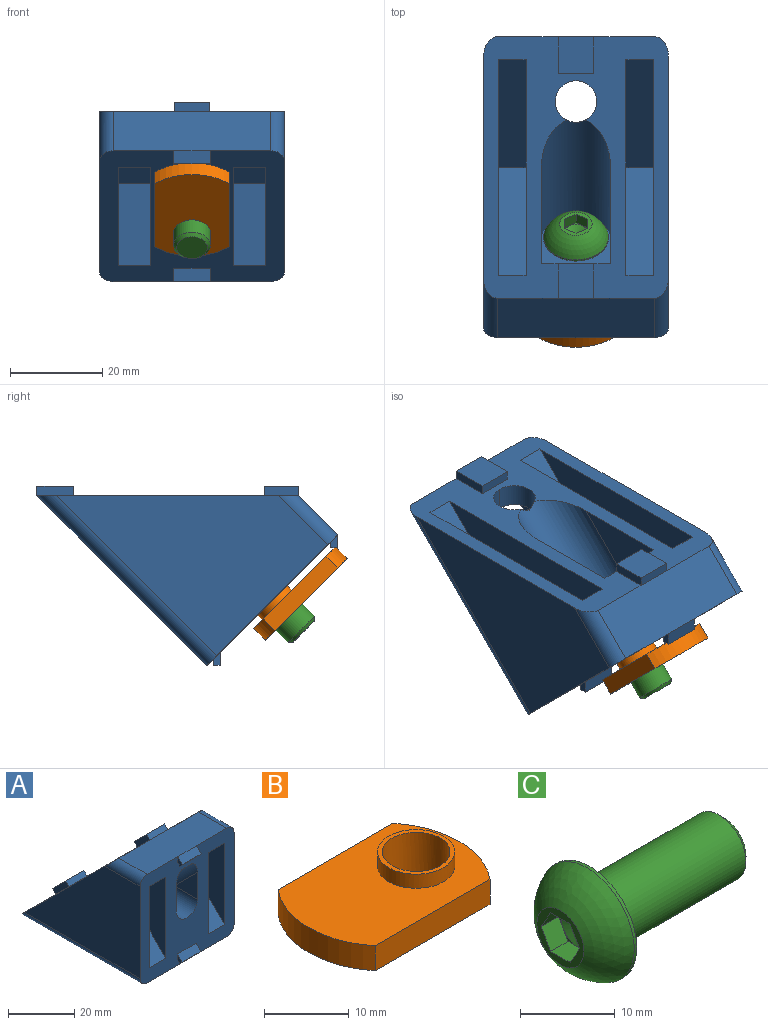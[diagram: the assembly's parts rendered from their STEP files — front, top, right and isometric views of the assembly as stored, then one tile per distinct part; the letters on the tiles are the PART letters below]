
ASSEMBLY  parts=3 mates=2
PART A: 65 faces, bbox 40x55.6x46.7 mm
  f0: plane 7.7x5.25mm, normal (0,0.71,0.71), area 57.2mm2, adj f2,f14,f18,f19
  f1: plane 8x1.06mm, normal (0,-0.71,-0.71), area 12mm2, adj f29,f30,f31,f32
  f2: plane 7.7x1.41mm, normal (0,-0.71,0.71), area 15.4mm2, adj f0,f14,f18,f36
  f3: plane 8x1.06mm, normal (0,-0.71,-0.71), area 12mm2, adj f4,f37,f38,f39
  f4: plane 8x2mm, normal (0,-0.71,0.71), area 22.6mm2, adj f3,f36,f37,f39
  f5: plane 17.5x7mm, normal (0,-1,0), area 122.5mm2, adj f40,f41,f42,f43
  f6: plane 17.5x7mm, normal (0,-1,0), area 122.5mm2, adj f44,f45,f46,f47
  f7: cylinder r=4.5mm len=2.03mm, axis (0,1,0), area 0.2mm2, adj f8,f51
  f8: plane 15x15mm, normal (0,1,0), area 135.3mm2, adj f7,f12,f13,f19,f20,f48,f50,f51
  f9: plane 7.7x5.66mm, normal (0,0.71,0.71), area 61.6mm2, adj f15,f16,f17,f59
  f10: cylinder r=4.5mm len=9.9mm, axis (0,-0.71,-0.71), area 69.6mm2, adj f11,f12,f58,f60
  f11: cylinder r=4.5mm len=9.9mm, axis (0,-0.71,-0.71), area 69.6mm2, adj f10,f12,f58,f60
  f12: cylinder r=7.5mm len=29.24mm, axis (0,1,0), area 627.8mm2, adj f8,f10,f11,f13,f20,f60
  f13: plane 22x14.75mm, normal (1,0,0), area 189.4mm2, adj f8,f12,f19,f60
  f14: plane 6.66x6.66mm, normal (-1,0,0), area 14.8mm2, adj f0,f2,f19,f60
  f15: plane 7.07x7.07mm, normal (-1,0,0), area 16mm2, adj f9,f16,f59,f60
  f16: plane 7.7x1.41mm, normal (0,-0.71,0.71), area 15.4mm2, adj f9,f15,f17,f60
  f17: plane 7.07x7.07mm, normal (1,0,0), area 16mm2, adj f9,f16,f59,f60
  f18: plane 6.66x6.66mm, normal (1,0,0), area 14.8mm2, adj f0,f2,f19,f60
  f19: plane 15x8.66mm, normal (0,0.71,-0.71), area 169.2mm2, adj f0,f8,f13,f14,f18,f20,f60
  f20: plane 22x14.75mm, normal (-1,0,0), area 189.4mm2, adj f8,f12,f19,f60
  f21: plane 33x6mm, normal (0,0,1), area 198mm2, adj f22,f23,f24,f60
  f22: plane 33x33mm, normal (1,0,0), area 544.5mm2, adj f21,f23,f60
  f23: plane 33x6mm, normal (0,1,0), area 198mm2, adj f21,f22,f24,f60
  f24: plane 33x33mm, normal (-1,0,0), area 544.5mm2, adj f21,f23,f60
  f25: plane 33x6mm, normal (0,0,1), area 198mm2, adj f26,f27,f28,f60
  f26: plane 33x33mm, normal (1,0,0), area 544.5mm2, adj f25,f27,f60
  f27: plane 33x6mm, normal (0,1,0), area 198mm2, adj f25,f26,f28,f60
  f28: plane 33x33mm, normal (-1,0,0), area 544.5mm2, adj f25,f27,f60
  f29: plane 3.06x2mm, normal (-1,0,0), area 3.1mm2, adj f1,f30,f32,f62
  f30: plane 8x0.94mm, normal (0,0.71,-0.71), area 10.6mm2, adj f1,f29,f31,f62
  f31: plane 3.06x2mm, normal (1,0,0), area 3.1mm2, adj f1,f30,f32,f62
  f32: plane 8x2mm, normal (0,-0.71,0.71), area 22.6mm2, adj f1,f29,f31,f62
  f33: cylinder r=3mm len=15mm, axis (0,1,0), area 61.7mm2, adj f34,f36,f60,f62
  f34: plane 49x34mm, normal (1,0,0), area 1088mm2, adj f33,f60,f61,f62
  f35: cylinder r=3mm len=15mm, axis (0,1,0), area 61.7mm2, adj f36,f54,f60,f62
  f36: plane 34x12mm, normal (0,0,1), area 408mm2, adj f2,f4,f33,f35,f60,f62
  f37: plane 3.06x2mm, normal (-1,0,0), area 3.1mm2, adj f3,f4,f38,f62
  f38: plane 8x0.94mm, normal (0,0.71,-0.71), area 10.6mm2, adj f3,f37,f39,f62
  f39: plane 3.06x2mm, normal (1,0,0), area 3.1mm2, adj f3,f4,f38,f62
  f40: plane 30x12.5mm, normal (1,0,0), area 296.9mm2, adj f5,f41,f43,f62
  f41: plane 12.5x12.5mm, normal (0,-0.71,0.71), area 123.7mm2, adj f5,f40,f42,f62
  f42: plane 30x12.5mm, normal (-1,0,0), area 296.9mm2, adj f5,f41,f43,f62
  f43: plane 12.5x7mm, normal (0,0,-1), area 87.5mm2, adj f5,f40,f42,f62
  f44: plane 30x12.5mm, normal (1,0,0), area 296.9mm2, adj f6,f45,f47,f62
  f45: plane 12.5x12.5mm, normal (0,-0.71,0.71), area 123.7mm2, adj f6,f44,f46,f62
  f46: plane 30x12.5mm, normal (-1,0,0), area 296.9mm2, adj f6,f45,f47,f62
  f47: plane 12.5x7mm, normal (0,0,-1), area 87.5mm2, adj f6,f44,f46,f62
  f48: cylinder r=4.5mm len=10mm, axis (0,1,0), area 141.4mm2, adj f8,f49,f53,f62
  f49: plane 10x10mm, normal (-1,0,0), area 50mm2, adj f48,f50,f62
  f50: cylinder r=3.1mm len=14.38mm, axis (0,-0.71,0.71), area 68.9mm2, adj f8,f49,f51,f62
  f51: plane 10x10mm, normal (0,-0.71,-0.71), area 39.4mm2, adj f7,f8,f50,f52,f62
  f52: cylinder r=3.1mm len=14.38mm, axis (0,-0.71,0.71), area 68.9mm2, adj f8,f51,f53,f62
  f53: plane 10x10mm, normal (1,0,0), area 50mm2, adj f48,f52,f62
  f54: plane 49x34mm, normal (-1,0,0), area 1088mm2, adj f35,f60,f62,f63
  f55: plane 12.73x6.36mm, normal (1,0,0), area 40.5mm2, adj f56,f58,f64
  f56: cylinder r=7.5mm len=16.99mm, axis (0,-0.71,-0.71), area 324.6mm2, adj f55,f57,f58,f64
  f57: plane 12.73x6.36mm, normal (-1,0,0), area 40.5mm2, adj f56,f58,f64
  f58: plane 15x11.67mm, normal (0,-0.71,-0.71), area 159.7mm2, adj f10,f11,f55,f56,f57,f64
  f59: plane 7.7x1.41mm, normal (0,0.71,-0.71), area 15.4mm2, adj f9,f15,f17,f64
  f60: plane 40x40mm, normal (0,0.71,0.71), area 1073.7mm2, adj f10,f11,f12,f13,f14,f15,f16,f17
  f61: cylinder r=3mm len=52mm, axis (0,1,0), area 239.9mm2, adj f34,f60,f62,f64
  f62: plane 40x40mm, normal (0,-1,0), area 982.9mm2, adj f29,f30,f31,f32,f33,f34,f35,f36
  f63: cylinder r=3mm len=52mm, axis (0,1,0), area 239.9mm2, adj f54,f60,f62,f64
  f64: plane 52x34mm, normal (0,0,-1), area 1452.1mm2, adj f55,f56,f57,f58,f59,f60,f61,f62
PART B: 9 faces, bbox 25x16.2x5.6 mm
  f0: cylinder r=12.7mm len=16.19mm, axis (0,0,1), area 63.3mm2, adj f1,f3,f4,f5
  f1: plane 19.16x3.61mm, normal (0,-1,0), area 69.1mm2, adj f0,f2,f4,f5
  f2: cylinder r=12.7mm len=16.19mm, axis (0,0,1), area 63.3mm2, adj f1,f3,f4,f5
  f3: plane 19.16x3.61mm, normal (0,1,0), area 69.1mm2, adj f0,f2,f4,f5
  f4: plane 24.99x16.19mm, normal (0,0,-1), area 324.6mm2, adj f0,f1,f2,f3,f8
  f5: plane 24.99x16.19mm, normal (0,0,1), area 309.5mm2, adj f0,f1,f2,f3,f6
  f6: cylinder r=4.56mm len=9.12mm, axis (0,0,-1), area 58.2mm2, adj f5,f7
  f7: plane 9.12x9.12mm, normal (0,0,1), area 15mm2, adj f6,f8
  f8: cylinder r=4mm len=8mm, axis (0,0,-1), area 141.7mm2, adj f4,f7
PART C: 21 faces, bbox 24.4x14x14 mm
  f0: plane 7x7mm, normal (-1,0,0), area 16.8mm2, adj f1,f8,f9,f10,f11,f12,f13
  f1: sphere r=7.45mm, area 188.3mm2, adj f0,f2
  f2: cylinder r=7mm len=14mm, axis (-1,0,0), area 16.7mm2, adj f1,f3
  f3: plane 14x14mm, normal (1,0,0), area 93.1mm2, adj f2,f7
  f4: cylinder r=4mm len=18.91mm, axis (-1,0,0), area 475.2mm2, adj f5,f7
  f5: cone r=3.31mm half-angle=45deg, axis (-1,0,0), area 22.4mm2, adj f4,f6
  f6: plane 6.62x6.62mm, normal (1,0,0), area 34.4mm2, adj f5
  f7: torus R=4.4mm, axis (-1,0,0), area 16.4mm2, adj f3,f4
  f8: plane 2.6x2.5mm, normal (0,0.87,-0.5), area 7.5mm2, adj f0,f9,f13,f18,f19
  f9: plane 2.6x2.5mm, normal (0,0.87,0.5), area 7.5mm2, adj f0,f8,f10,f17,f18
  f10: plane 2.89x2.6mm, normal (0,0,1), area 7.5mm2, adj f0,f9,f11,f16,f17
  f11: plane 2.6x2.5mm, normal (0,-0.87,0.5), area 7.5mm2, adj f0,f10,f12,f15,f16
  f12: plane 2.6x2.5mm, normal (0,-0.87,-0.5), area 7.5mm2, adj f0,f11,f13,f14,f15
  f13: plane 2.89x2.6mm, normal (0,0,-1), area 7.5mm2, adj f0,f8,f12,f14,f19
  f14: plane 2.17x1.25mm, normal (-1,0,0), area 0.3mm2, adj f12,f13,f20
  f15: plane 2.5x0.72mm, normal (-1,0,0), area 0.3mm2, adj f11,f12,f20
  f16: plane 2.17x1.25mm, normal (-1,0,0), area 0.3mm2, adj f10,f11,f20
  f17: plane 2.17x1.25mm, normal (-1,0,0), area 0.3mm2, adj f9,f10,f20
  f18: plane 2.5x0.72mm, normal (-1,0,0), area 0.3mm2, adj f8,f9,f20
  f19: plane 2.17x1.25mm, normal (-1,0,0), area 0.3mm2, adj f8,f13,f20
  f20: cone r=0mm half-angle=60deg, axis (-1,0,0), area 22.7mm2, adj f14,f15,f16,f17,f18,f19
PLACE A rot(axis=(1,0,0),45deg) t=(29.37,-79.07,-53.78)mm
PLACE B rot(axis=(-0.36,0.36,0.86),98.4deg) t=(37.47,-76.35,-61.16)mm
PLACE C rot(axis=(0.68,-0.28,-0.68),148.6deg) t=(29.37,-68.6,-43.32)mm
MATE fastened C.f2 <-> A.f7  axis (0,0.71,0.71) through (29.37,-72,-46.71)mm
MATE fastened B.f6 <-> C.f2  axis (0,-0.71,-0.71) through (29.37,-78.68,-53.4)mm
